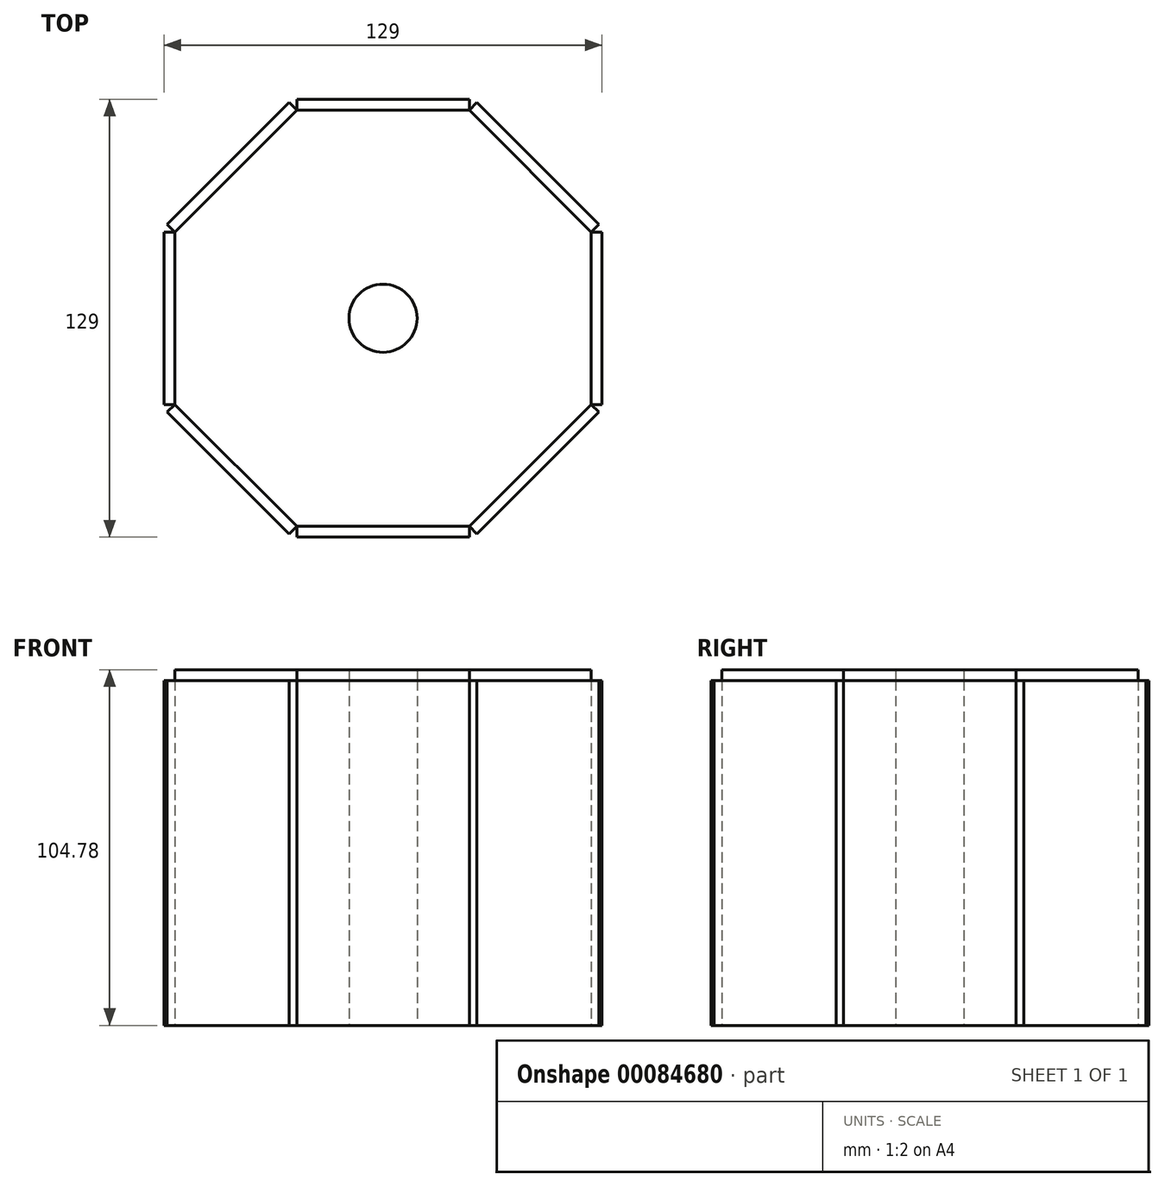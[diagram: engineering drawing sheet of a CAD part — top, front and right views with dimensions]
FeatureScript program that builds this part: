
annotation { "Feature Type Name" : "Feature", "Feature Type Description" : "" }
export const myFeature = defineFeature(function(context is Context, id is Id, definition is map)
    precondition{}
    {
        {
            var Q0;
            Q0=qCreatedBy(makeId("Top.planeOp"),FACE);
            var sketch = newSketch(context, id + "F0", { "sketchPlane" : qUnion([Q0])});
            skLineSegment(sketch, "E0", {"start": v(-25.4, 0) * mm, "end": v(25.4, 0) * mm});
            skLineSegment(sketch, "E1", {"start": v(-25.4, 0) * mm, "end": v(-61.32, 35.92) * mm});
            skLineSegment(sketch, "E2", {"start": v(-61.32, 35.92) * mm, "end": v(-61.32, 86.72) * mm});
            skLineSegment(sketch, "E3", {"start": v(-61.32, 86.72) * mm, "end": v(-25.4, 122.64) * mm});
            skLineSegment(sketch, "E4", {"start": v(-25.4, 122.64) * mm, "end": v(25.4, 122.64) * mm});
            skLineSegment(sketch, "E5", {"start": v(25.4, 122.64) * mm, "end": v(61.32, 86.72) * mm});
            skLineSegment(sketch, "E6", {"start": v(61.32, 86.72) * mm, "end": v(61.32, 35.92) * mm});
            skLineSegment(sketch, "E7", {"start": v(61.32, 35.92) * mm, "end": v(25.4, 0) * mm});
            skLineSegment(sketch, "E8", {"start": v(-61.32, 61.32) * mm, "end": v(61.32, 61.32) * mm});
            skLineSegment(sketch, "E9", {"start": v(0, 61.32) * mm, "end": v(0, 122.64) * mm});
            skPoint(sketch, "E9.endSnap0", {"position": v(0, 122.64) * mm});
            skLineSegment(sketch, "E10", {"start": v(0, 61.32) * mm, "end": v(0, 0) * mm});
            skPoint(sketch, "E11", {"position": v(0, 61.32) * mm});
            skCircle(sketch, "E12", {"center": v(0, 61.32) * mm, "radius": 10.02 * mm});
            skSolve(sketch);
        }
        {
            var Q0;
            {var subQ5=sQuery(id+"F0.wireOp",EDGE,"E3");Q0=makeQuery(id+"F0.imprint","IMPRINT",FACE,{"disambiguationData":[TD([[makeQuery(id+"F0.imprint","IMPRINT",EDGE,{"derivedFrom":subQ5}),-1.0]])]});}
            var Q1;
            {var subQ1=sQuery(id+"F0.wireOp",EDGE,"E5");Q1=makeQuery(id+"F0.imprint","IMPRINT",FACE,{"disambiguationData":[TD([[makeQuery(id+"F0.imprint","IMPRINT",EDGE,{"derivedFrom":subQ1}),-1.0]])]});}
            var Q2;
            {var subQ4=sQuery(id+"F0.wireOp",EDGE,"E7");Q2=makeQuery(id+"F0.imprint","IMPRINT",FACE,{"disambiguationData":[TD([[makeQuery(id+"F0.imprint","IMPRINT",EDGE,{"derivedFrom":subQ4}),-1.0]])]});}
            var Q3;
            {var subQ1=sQuery(id+"F0.wireOp",EDGE,"E1");Q3=makeQuery(id+"F0.imprint","IMPRINT",FACE,{"disambiguationData":[TD([[makeQuery(id+"F0.imprint","IMPRINT",EDGE,{"derivedFrom":subQ1}),-1.0]])]});}
            extrude(context, id + "F1", {"entities" : qUnion([Q0, Q1, Q2, Q3]), "depth" : 101.6 * mm});
        }
        {
            var Q0;
            Q0=makeQuery(id+"F1.opExtrude","SWEPT_FACE",FACE,{"disambiguationData":[OSD([sQuery(id+"F0.wireOp",EDGE,"E5")])]});
            extrude(context, id + "F2", {"entities" : qUnion([Q0]), "depth" : 3.17 * mm});
        }
        {
            var Q0;
            Q0=makeQuery(id+"F2.opExtrude","SWEPT_BODY",BODY,{"disambiguationData":[OSD([sQuery(id+"F0.wireOp",EDGE,"E5")])]});
            var Q1;
            Q1=sQuery(id+"F0.wireOp",EDGE,"E12");
            circularPattern(context, id + "F3", {"entities" : qUnion([Q0]), "axis" : qUnion([Q1]), "angle" : 360 * degree, "instanceCount" : 8, "equalSpace" : true});
        }
        {
            var Q0;
            Q0=makeQuery(id+"F1.opExtrude","CAP_FACE",FACE,{"disambiguationData":[OSD([sQuery(id+"F0.wireOp",EDGE,"E0"),sQuery(id+"F0.wireOp",EDGE,"E1"),sQuery(id+"F0.wireOp",EDGE,"E2"),sQuery(id+"F0.wireOp",EDGE,"E3"),sQuery(id+"F0.wireOp",EDGE,"E4"),sQuery(id+"F0.wireOp",EDGE,"E5"),sQuery(id+"F0.wireOp",EDGE,"E6"),sQuery(id+"F0.wireOp",EDGE,"E7"),sQuery(id+"F0.wireOp",EDGE,"E12")])],"isStart":false});
            extrude(context, id + "F4", {"entities" : qUnion([Q0]), "depth" : 3.17 * mm});
        }
    });
